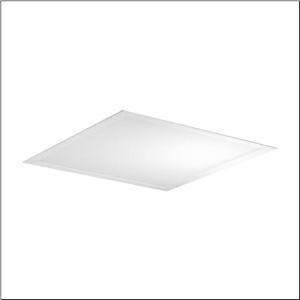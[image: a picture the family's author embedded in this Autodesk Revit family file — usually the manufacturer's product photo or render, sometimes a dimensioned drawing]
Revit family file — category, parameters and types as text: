
# Revit family: apollon_r__31_square_51mp11wd2342_576e
name_source: partatom
category: Lighting Fixtures
units: mm (PartAtom-declared; Revit-internal decimal feet)

## family parameters
Cut with Voids When Loaded = No
Host = Face
Light Source = No
Part Type = Normal
Room Calculation Point = No
Round Connector Dimension = Use Diameter
Shared = No

## types (1)
- Apollon® 31 square (1 x LED, 3800 lm, 27.5 W, 3000K)
    Apparent Load = 28 VA
    CIE Flux Codes = 61 87 97 100 100
    Color Rendering = 80
    Color Temperature = 3000K
    Default Elevation = 1800 mm
    Description = Apollon® 31 square, office luminaire, primary optical cover: micro prismatic cover, of PMMA, CAT 2 (L<= 3000cd/m²), light emission: direct distribution, primary light characteristic: symmetric, installation type: lay-in mounting, LED, rated luminous flux: 3.800lm, luminous efficacy: 138lm/W, light colour: 830, colour temperature: 3000K, with terminal, 5-pole, mains connection: 220..240V, AC/DC, 0/50..60Hz, rated input power: 28W, housing, of aluminium, traffic white (RAL 9016), module: M625, length: 620mm, width: 620mm, height: 32mm, housing upper side, of sheet steel, galvanised, protection rating (complete): IP20, protection rating (on room side): IP40, insulation class (complete): insulation class II (safety insulation), certification: CE, ENEC, impact resistance: IK03, permissible operating ambient temperature: -20..+40°C, permissible storage temperature: -20..+60°C, packaging unit: 1 piece
    Height = 0 mm  [stored 0 ft]
    Lamp = 1 x LED
    Lamp Light Flux = 3800 lm
    Lamp Power = 27.5 W
    Lamp count = 1
    Length = 620 mm
    Luminous efficacy = 138 lm/W
    Manufacturer = Siteco
    ModVariant = No
    Model = 51MP11WD2342
    Mounting Place = Ceiling
    Mounting Type = Recessed
    Number of Poles = 1
    OnlyDefault = Yes
    Power Factor = 1
    Product Name = Apollon® 31 square
    Product group = office luminaire | ceiling recessed
    ProductGroupID = 401
    Protection Class = Protection class II
    Protection Degree = IP 20
    RLX_Detail_Level = 1
    RLX_Emergency_Light_Flux = 0 lm
    RLX_Emergency_Type = 0
    RLX_Emergency_Type_DB = No
    RlxData = <blob elided: 12937 chars, md5=7c2f2b58>
    Socket = socket
    Standby Power = 0 W
    System Light Flux = 3800 lm
    System Power = 28 W
    Type Comments = Product without accessories
    Type Image = l_1291039.jpg
    URL = http://relux.com
    VarID = ---
    Voltage = 0 V
    Weight = 0.00 kg
    Width = 620 mm

note: [stored X ft] marks values corroborated as IEEE doubles in the binary element streams (Revit-internal decimal feet)

## geometry (parser evidence)
native form markers: Sweep x9
no freeform markers — native parametric forms only
